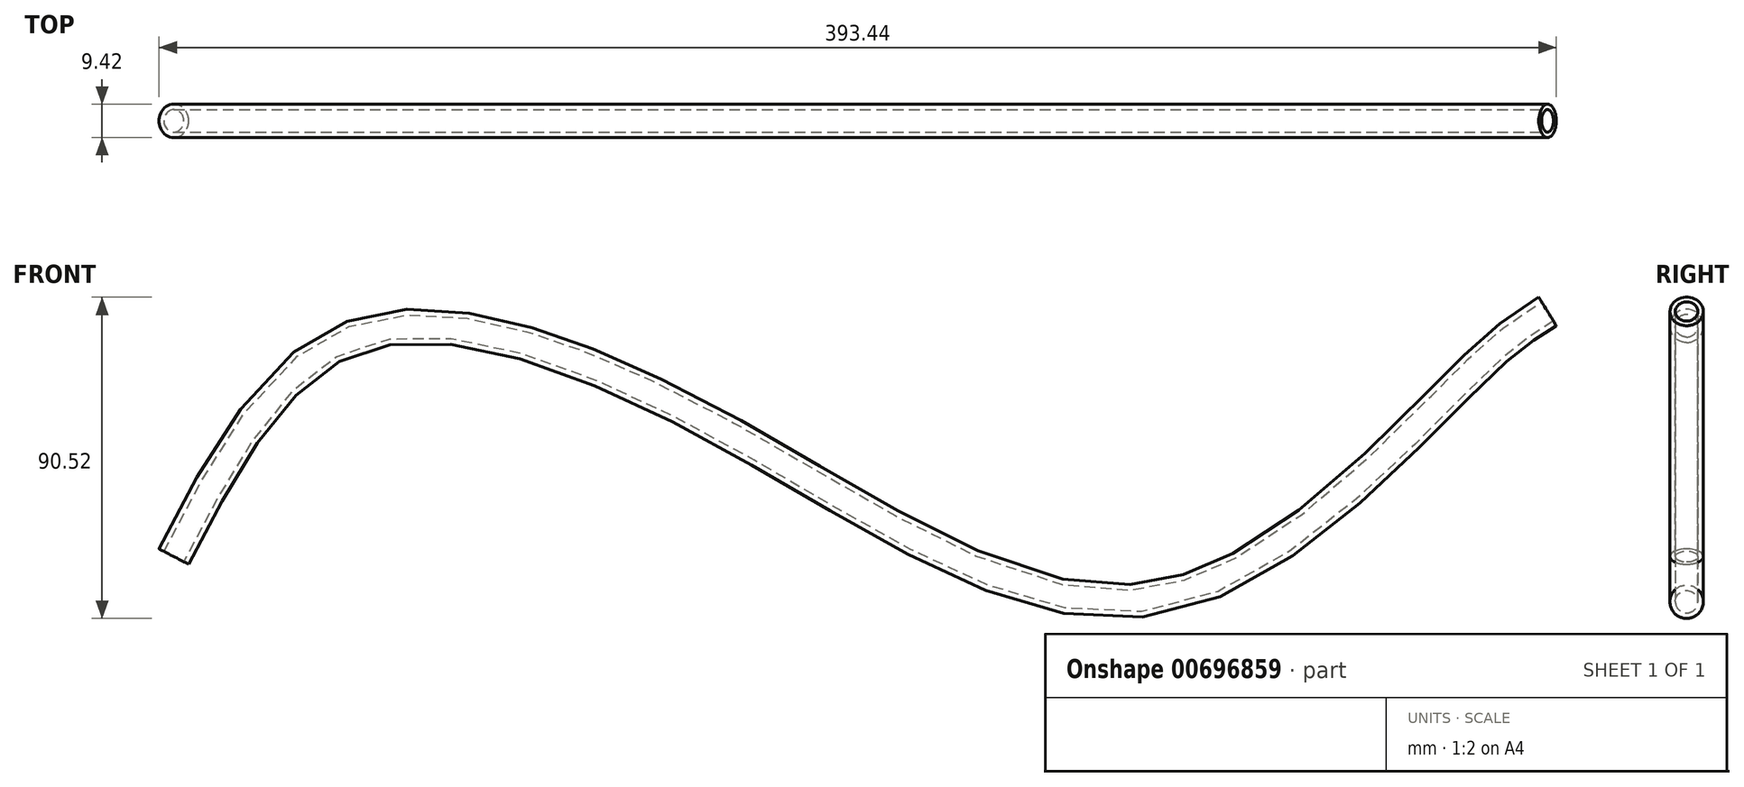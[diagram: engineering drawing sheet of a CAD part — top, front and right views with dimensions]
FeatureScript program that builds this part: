
annotation { "Feature Type Name" : "Feature", "Feature Type Description" : "" }
export const myFeature = defineFeature(function(context is Context, id is Id, definition is map)
    precondition{}
    {
        {
            var Q0;
            Q0=qCreatedBy(makeId("Front.planeOp"),FACE);
            var sketch = newSketch(context, id + "F0", { "sketchPlane" : qUnion([Q0])});
            skFitSpline(sketch, "E0", {"points": [v(-144.8, -11.85) * mm, v(-93.39, 50.4) * mm, v(13.46, 21.9) * mm, v(134.76, -23.1) * mm, v(223.13, 42.78) * mm, v(242, 57.24) * mm], "startDerivative": vector(215.87, 417.65) * mm, "endDerivative": vector(146.76, 90.02) * mm});
            skSolve(sketch);
        }
        {
            var Q0;
            Q0=sQuery(id+"F0.wireOp",EDGE,"E0");
            var Q1;
            Q1=sQuery(id+"F0.wireOp",VERTEX,"E0.end");
            cPlane(context, id + "F1", {"entities" : qUnion([Q0, Q1]), "cplaneType" : CPlaneType.CURVE_POINT, "offset" : 25 * mm, "width" : 150 * mm, "height" : 150 * mm});
        }
        {
            var Q0;
            Q0=qCreatedBy(id+"F1.planeOp",FACE);
            var sketch = newSketch(context, id + "F2", { "sketchPlane" : qUnion([Q0])});
            skCircle(sketch, "E1", {"center": v(0, -77.74) * mm, "radius": 3.17 * mm});
            skCircle(sketch, "E2", {"center": v(0, -77.74) * mm, "radius": 4.7 * mm});
            skSolve(sketch);
        }
        {
            var Q0;
            Q0=makeQuery(id+"F2.imprint","IMPRINT",FACE,{"disambiguationData":[TD([[makeQuery(id+"F2.imprint","IMPRINT",EDGE,{"derivedFrom":sQuery(id+"F2.wireOp",EDGE,"E1")}),-1.0]])]});
            var Q1;
            Q1=sQuery(id+"F0.wireOp",EDGE,"E0");
            sweep(context, id + "F3", {"profiles" : qUnion([Q0]), "path" : qUnion([Q1])});
        }
    });
